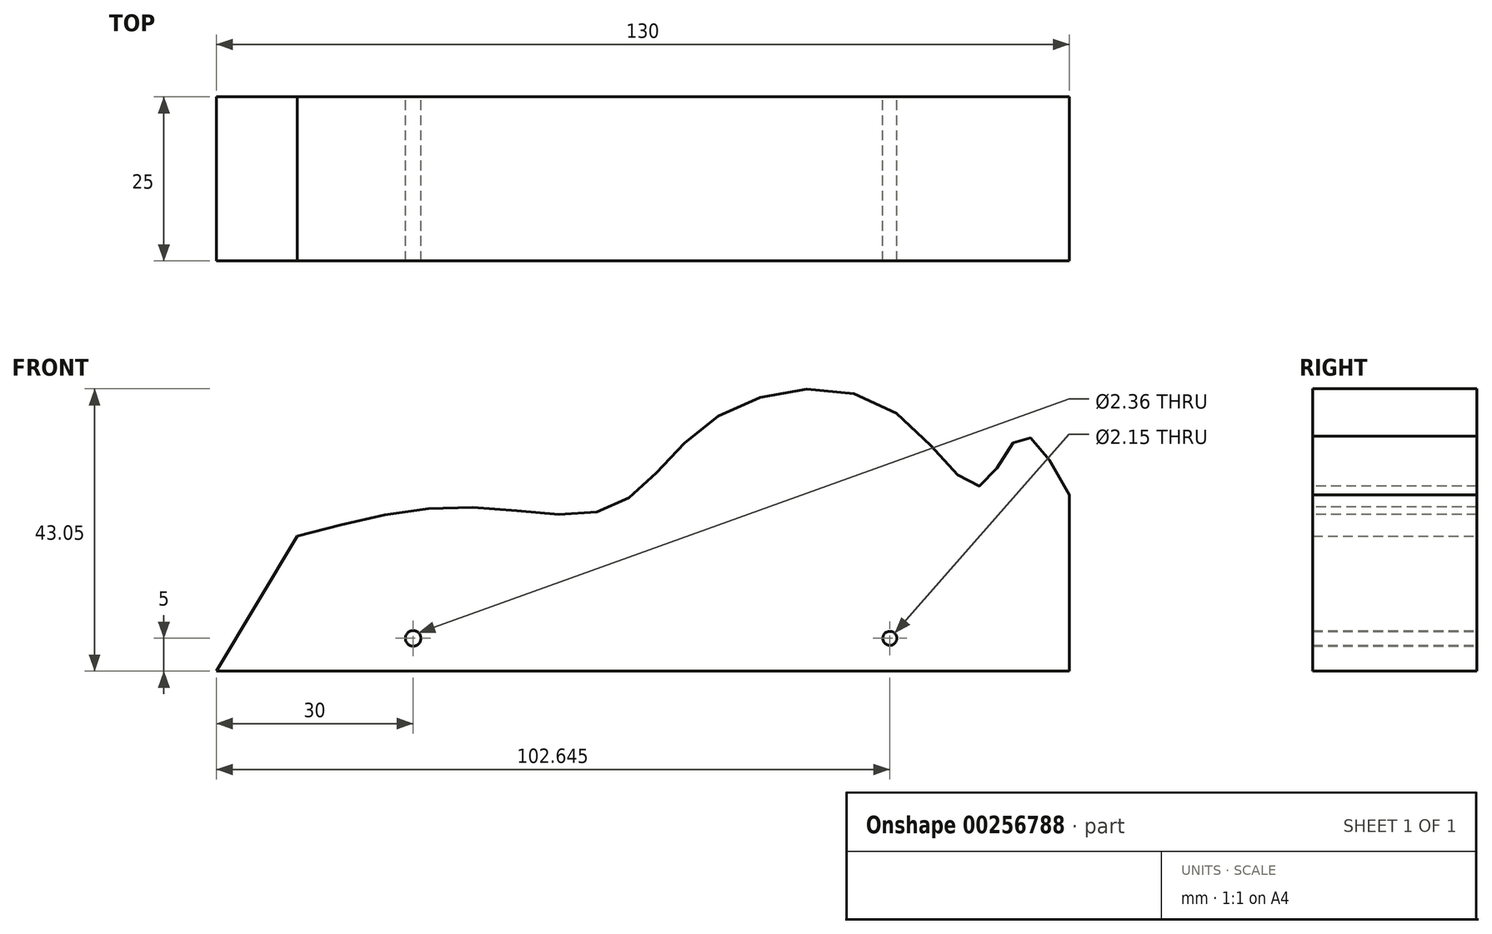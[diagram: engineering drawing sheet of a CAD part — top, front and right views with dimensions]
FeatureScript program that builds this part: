
annotation { "Feature Type Name" : "Feature", "Feature Type Description" : "" }
export const myFeature = defineFeature(function(context is Context, id is Id, definition is map)
    precondition{}
    {
        {
            var Q0;
            Q0=qCreatedBy(makeId("Front.planeOp"),FACE);
            var sketch = newSketch(context, id + "F0", { "sketchPlane" : qUnion([Q0])});
            skLineSegment(sketch, "E0.bottom", {"start": v(-50, -25) * mm, "end": v(50, -25) * mm});
            skLineSegment(sketch, "E0.top", {"start": v(-50, 25) * mm, "end": v(50, 25) * mm});
            skLineSegment(sketch, "E0.right", {"start": v(50, -25) * mm, "end": v(50, 25) * mm});
            skPoint(sketch, "E0.middle", {"position": v(0, 0) * mm});
            skLineSegment(sketch, "E1", {"start": v(-50, -25) * mm, "end": v(-80, -25) * mm});
            skLineSegment(sketch, "E2", {"start": v(-80, -25) * mm, "end": v(-50, 25) * mm});
            skLineSegment(sketch, "E3", {"start": v(50, -25) * mm, "end": v(22.65, -25) * mm});
            skFitSpline(sketch, "E4", {"points": [v(-67.64, -4.4) * mm, v(-41.59, 0) * mm, v(-19.64, 0) * mm, v(-4.1, 13.5) * mm, v(22.62, 15) * mm, v(36.48, 3.27) * mm, v(42.5, 10.7) * mm, v(50, 1.86) * mm], "startDerivative": vector(152.65, 40.78) * mm, "endDerivative": vector(70.27, -131.38) * mm});
            skCircle(sketch, "E5", {"center": v(-50, -20) * mm, "radius": 1.18 * mm});
            skCircle(sketch, "E6", {"center": v(22.65, -20) * mm, "radius": 1.07 * mm});
            skSolve(sketch);
        }
        {
            var Q0;
            Q0=makeQuery(id+"F0.imprint","IMPRINT",FACE,{"disambiguationData":[TD([[makeQuery(id+"F0.imprint","IMPRINT",EDGE,{"derivedFrom":sQuery(id+"F0.wireOp",EDGE,"E0.bottom")}),1.0]])]});
            extrude(context, id + "F1", {"entities" : qUnion([Q0]), "depth" : 25 * mm});
        }
        {
            var Q0;
            Q0=makeQuery(id+"F0.imprint","IMPRINT",FACE,{"disambiguationData":[TD([[makeQuery(id+"F0.imprint","IMPRINT",EDGE,{"derivedFrom":sQuery(id+"F0.wireOp",EDGE,"E0.bottom")}),1.0]])]});
            extrude(context, id + "F2", {"entities" : qUnion([Q0]), "operationType" : NewBodyOperationType.ADD, "depth" : 25 * mm});
        }
        {
            var Q0;
            {var subQ0=sQuery(id+"F0.wireOp",EDGE,"E0.top");Q0=makeQuery(id+"F0.imprint","IMPRINT",FACE,{"disambiguationData":[TD([[makeQuery(id+"F0.imprint","IMPRINT",EDGE,{"derivedFrom":subQ0}),-1.0]])]});}
            extrude(context, id + "F3", {"entities" : qUnion([Q0]), "operationType" : NewBodyOperationType.REMOVE, "endBound" : BoundingType.THROUGH_ALL, "oppositeDirection" : true, "depth" : 25 * mm});
        }
    });
